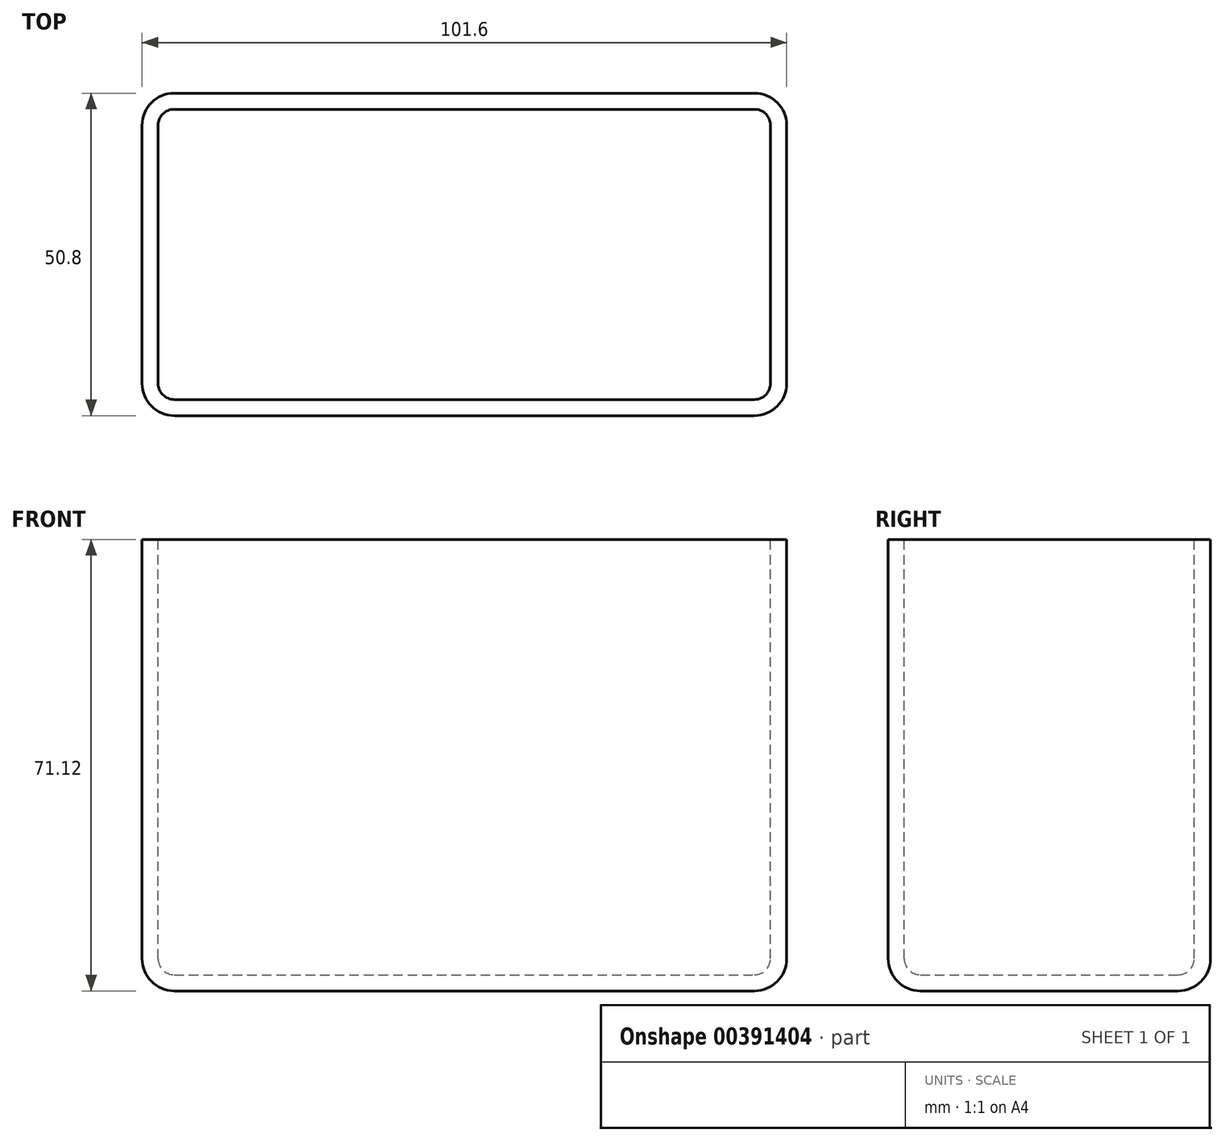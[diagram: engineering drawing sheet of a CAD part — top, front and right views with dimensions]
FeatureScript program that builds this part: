
annotation { "Feature Type Name" : "Feature", "Feature Type Description" : "" }
export const myFeature = defineFeature(function(context is Context, id is Id, definition is map)
    precondition{}
    {
        {
            var Q0;
            Q0=qCreatedBy(makeId("Top.planeOp"),FACE);
            var sketch = newSketch(context, id + "F0", { "sketchPlane" : qUnion([Q0])});
            skLineSegment(sketch, "E0.bottom", {"start": v(-50.8, -25.4) * mm, "end": v(50.8, -25.4) * mm});
            skLineSegment(sketch, "E0.top", {"start": v(-50.8, 25.4) * mm, "end": v(50.8, 25.4) * mm});
            skLineSegment(sketch, "E0.left", {"start": v(-50.8, -25.4) * mm, "end": v(-50.8, 25.4) * mm});
            skLineSegment(sketch, "E0.right", {"start": v(50.8, -25.4) * mm, "end": v(50.8, 25.4) * mm});
            skPoint(sketch, "E0.middle", {"position": v(0, 0) * mm});
            skSolve(sketch);
        }
        {
            var Q0;
            Q0 = qSketchRegion(id + "F0", true);
            extrude(context, id + "F1", {"entities" : qUnion([Q0]), "depth" : 76.2 * mm});
        }
        {
            var Q0;
            Q0=makeQuery(id+"F1.opExtrude","SWEPT_FACE",FACE,{"disambiguationData":[OSD([sQuery(id+"F0.wireOp",EDGE,"E0.bottom")])]});
            var Q1;
            Q1=makeQuery(id+"F1.opExtrude","SWEPT_FACE",FACE,{"disambiguationData":[OSD([sQuery(id+"F0.wireOp",EDGE,"E0.left")])]});
            var Q2;
            Q2=makeQuery(id+"F1.opExtrude","SWEPT_FACE",FACE,{"disambiguationData":[OSD([sQuery(id+"F0.wireOp",EDGE,"E0.top")])]});
            var Q3;
            Q3=makeQuery(id+"F1.opExtrude","SWEPT_FACE",FACE,{"disambiguationData":[OSD([sQuery(id+"F0.wireOp",EDGE,"E0.right")])]});
            var Q4;
            Q4=makeQuery(id+"F1.opExtrude","CAP_FACE",FACE,{"disambiguationData":[OSD([sQuery(id+"F0.wireOp",EDGE,"E0.bottom"),sQuery(id+"F0.wireOp",EDGE,"E0.top"),sQuery(id+"F0.wireOp",EDGE,"E0.left"),sQuery(id+"F0.wireOp",EDGE,"E0.right")])],"isStart":false});
            fillet(context, id + "F2", {"entities" : qUnion([Q0, Q1, Q2, Q3, Q4]), "radius" : 5.08 * mm, "tangentPropagation" : true, "allowEdgeOverflow" : false});
        }
        {
            var Q0;
            Q0=makeQuery(id+"F1.opExtrude","CAP_FACE",FACE,{"disambiguationData":[OSD([sQuery(id+"F0.wireOp",EDGE,"E0.bottom"),sQuery(id+"F0.wireOp",EDGE,"E0.top"),sQuery(id+"F0.wireOp",EDGE,"E0.left"),sQuery(id+"F0.wireOp",EDGE,"E0.right")])],"isStart":false});
            var Q1;
            {var subQ0=sQuery(id+"F0.wireOp",EDGE,"E0.top");Q1=makeQuery(id+"F2.opFillet","BLEND_FACE",FACE,{"disambiguationData":[OSD([subQ0]),TDD([makeQuery(id+"F1.opExtrude","CAP_EDGE",EDGE,{"disambiguationData":[OSD([subQ0])],"isStart":false})])]});}
            var Q2;
            {var subQ0=sQuery(id+"F0.wireOp",EDGE,"E0.left");var subQ1=sQuery(id+"F0.wireOp",EDGE,"E0.top");Q2=makeQuery(id+"F2.opFillet","BLEND_FACE",FACE,{"disambiguationData":[OSD([subQ1,subQ0]),TDD([makeQuery(id+"F1.opExtrude","CAP_VERTEX",VERTEX,{"disambiguationData":[OSD([subQ1,subQ0])],"isStart":false})])]});}
            var Q3;
            {var subQ0=sQuery(id+"F0.wireOp",EDGE,"E0.left");Q3=makeQuery(id+"F2.opFillet","BLEND_FACE",FACE,{"disambiguationData":[OSD([subQ0]),TDD([makeQuery(id+"F1.opExtrude","CAP_EDGE",EDGE,{"disambiguationData":[OSD([subQ0])],"isStart":false})])]});}
            var Q4;
            {var subQ0=sQuery(id+"F0.wireOp",EDGE,"E0.left");var subQ1=sQuery(id+"F0.wireOp",EDGE,"E0.bottom");Q4=makeQuery(id+"F2.opFillet","BLEND_FACE",FACE,{"disambiguationData":[OSD([subQ1,subQ0]),TDD([makeQuery(id+"F1.opExtrude","CAP_VERTEX",VERTEX,{"disambiguationData":[OSD([subQ1,subQ0])],"isStart":false})])]});}
            var Q5;
            {var subQ0=sQuery(id+"F0.wireOp",EDGE,"E0.bottom");Q5=makeQuery(id+"F2.opFillet","BLEND_FACE",FACE,{"disambiguationData":[OSD([subQ0]),TDD([makeQuery(id+"F1.opExtrude","CAP_EDGE",EDGE,{"disambiguationData":[OSD([subQ0])],"isStart":false})])]});}
            var Q6;
            {var subQ0=sQuery(id+"F0.wireOp",EDGE,"E0.right");var subQ1=sQuery(id+"F0.wireOp",EDGE,"E0.bottom");Q6=makeQuery(id+"F2.opFillet","BLEND_FACE",FACE,{"disambiguationData":[OSD([subQ1,subQ0]),TDD([makeQuery(id+"F1.opExtrude","CAP_VERTEX",VERTEX,{"disambiguationData":[OSD([subQ1,subQ0])],"isStart":false})])]});}
            var Q7;
            {var subQ0=sQuery(id+"F0.wireOp",EDGE,"E0.right");Q7=makeQuery(id+"F2.opFillet","BLEND_FACE",FACE,{"disambiguationData":[OSD([subQ0]),TDD([makeQuery(id+"F1.opExtrude","CAP_EDGE",EDGE,{"disambiguationData":[OSD([subQ0])],"isStart":false})])]});}
            var Q8;
            {var subQ0=sQuery(id+"F0.wireOp",EDGE,"E0.right");var subQ1=sQuery(id+"F0.wireOp",EDGE,"E0.top");Q8=makeQuery(id+"F2.opFillet","BLEND_FACE",FACE,{"disambiguationData":[OSD([subQ1,subQ0]),TDD([makeQuery(id+"F1.opExtrude","CAP_VERTEX",VERTEX,{"disambiguationData":[OSD([subQ1,subQ0])],"isStart":false})])]});}
            shell(context, id + "F3", {"entities" : qUnion([Q0, Q1, Q2, Q3, Q4, Q5, Q6, Q7, Q8]), "thickness" : 2.54 * mm});
        }
    });
